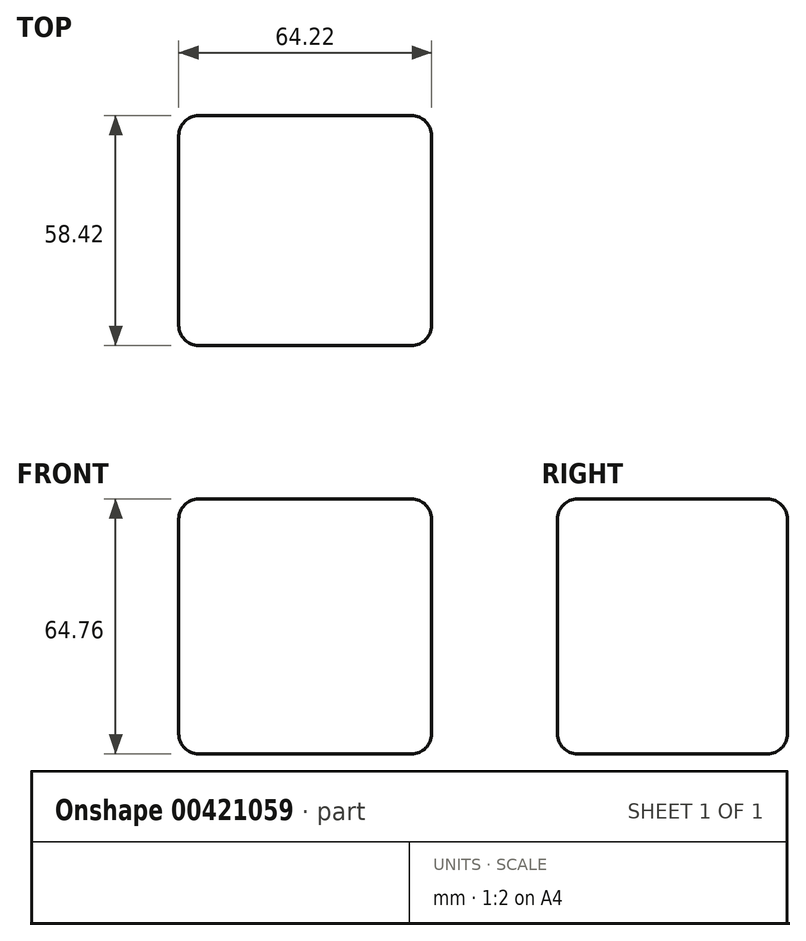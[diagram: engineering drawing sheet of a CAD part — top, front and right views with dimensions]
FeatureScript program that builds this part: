
annotation { "Feature Type Name" : "Feature", "Feature Type Description" : "" }
export const myFeature = defineFeature(function(context is Context, id is Id, definition is map)
    precondition{}
    {
        {
            var Q0;
            Q0=qCreatedBy(makeId("Front.planeOp"),FACE);
            var sketch = newSketch(context, id + "F0", { "sketchPlane" : qUnion([Q0])});
            skLineSegment(sketch, "E0.bottom", {"start": v(32.11, -32.38) * mm, "end": v(-32.11, -32.38) * mm});
            skLineSegment(sketch, "E0.top", {"start": v(32.11, 32.38) * mm, "end": v(-32.11, 32.38) * mm});
            skLineSegment(sketch, "E0.left", {"start": v(32.11, -32.38) * mm, "end": v(32.11, 32.38) * mm});
            skLineSegment(sketch, "E0.right", {"start": v(-32.11, -32.38) * mm, "end": v(-32.11, 32.38) * mm});
            skPoint(sketch, "E0.middle", {"position": v(0, 0) * mm});
            skSolve(sketch);
        }
        {
            var Q0;
            Q0=makeQuery(id+"F0.imprint","IMPRINT",FACE,{"disambiguationData":[TD([[makeQuery(id+"F0.imprint","IMPRINT",EDGE,{"derivedFrom":sQuery(id+"F0.wireOp",EDGE,"E0.bottom")}),-1.0]])]});
            extrude(context, id + "F1", {"entities" : qUnion([Q0]), "depth" : 58.42 * mm});
        }
        {
            var Q0;
            Q0=makeQuery(id+"F1.opExtrude","CAP_FACE",FACE,{"disambiguationData":[OSD([sQuery(id+"F0.wireOp",EDGE,"E0.bottom"),sQuery(id+"F0.wireOp",EDGE,"E0.top"),sQuery(id+"F0.wireOp",EDGE,"E0.left"),sQuery(id+"F0.wireOp",EDGE,"E0.right")])],"isStart":false});
            var Q1;
            Q1=makeQuery(id+"F1.opExtrude","SWEPT_FACE",FACE,{"disambiguationData":[OSD([sQuery(id+"F0.wireOp",EDGE,"E0.left")])]});
            var Q2;
            Q2=makeQuery(id+"F1.opExtrude","CAP_FACE",FACE,{"disambiguationData":[OSD([sQuery(id+"F0.wireOp",EDGE,"E0.bottom"),sQuery(id+"F0.wireOp",EDGE,"E0.top"),sQuery(id+"F0.wireOp",EDGE,"E0.left"),sQuery(id+"F0.wireOp",EDGE,"E0.right")])],"isStart":true});
            var Q3;
            Q3=makeQuery(id+"F1.opExtrude","SWEPT_FACE",FACE,{"disambiguationData":[OSD([sQuery(id+"F0.wireOp",EDGE,"E0.right")])]});
            fillet(context, id + "F2", {"entities" : qUnion([Q0, Q1, Q2, Q3]), "radius" : 5.08 * mm, "tangentPropagation" : true, "allowEdgeOverflow" : false});
        }
    });
